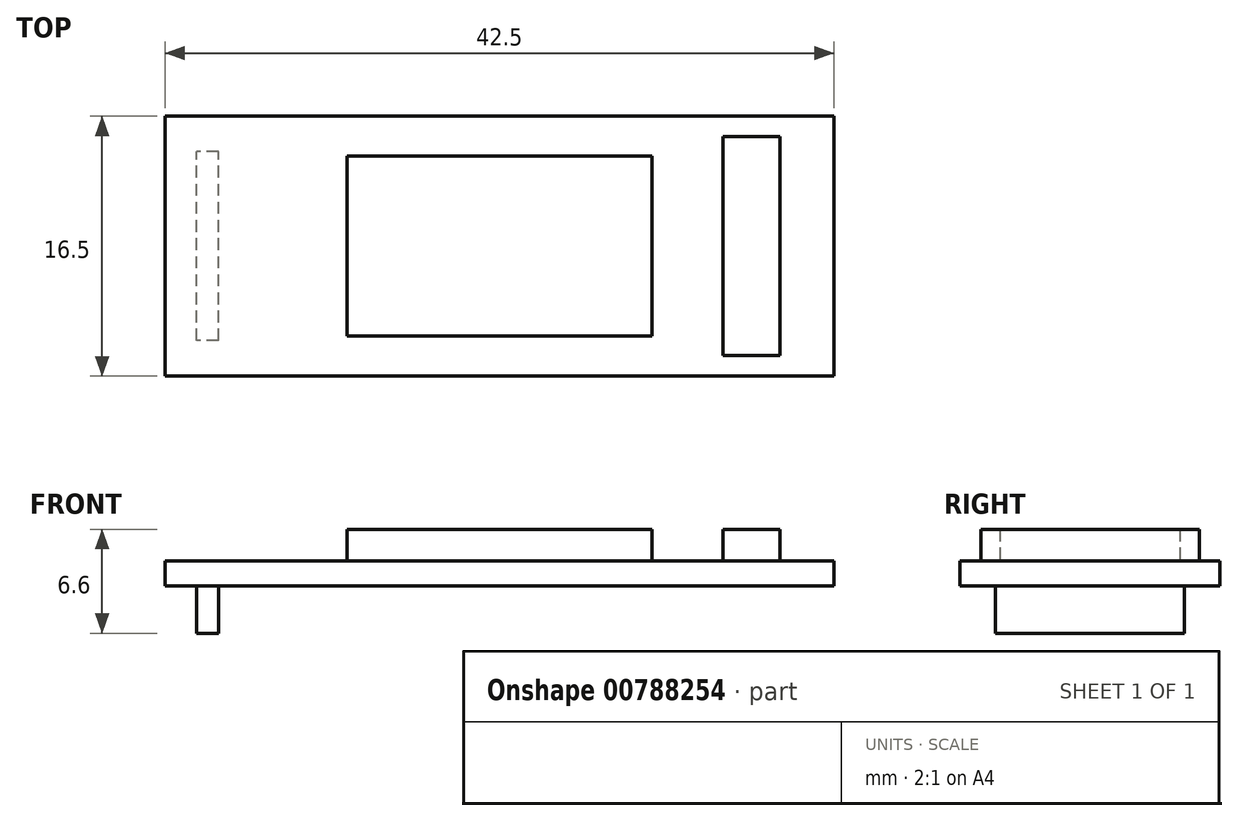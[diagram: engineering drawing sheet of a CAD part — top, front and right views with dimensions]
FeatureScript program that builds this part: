
annotation { "Feature Type Name" : "Feature", "Feature Type Description" : "" }
export const myFeature = defineFeature(function(context is Context, id is Id, definition is map)
    precondition{}
    {
        {
            var Q0;
            Q0=qCreatedBy(makeId("Top.planeOp"),FACE);
            var sketch = newSketch(context, id + "F0", { "sketchPlane" : qUnion([Q0])});
            skLineSegment(sketch, "E0.bottom", {"start": v(21.25, 8.25) * mm, "end": v(-21.25, 8.25) * mm});
            skLineSegment(sketch, "E0.top", {"start": v(21.25, -8.25) * mm, "end": v(-21.25, -8.25) * mm});
            skLineSegment(sketch, "E0.left", {"start": v(21.25, 8.25) * mm, "end": v(21.25, -8.25) * mm});
            skLineSegment(sketch, "E0.right", {"start": v(-21.25, 8.25) * mm, "end": v(-21.25, -8.25) * mm});
            skPoint(sketch, "E0.middle", {"position": v(0, 0) * mm});
            skSolve(sketch);
        }
        {
            var Q0;
            Q0=makeQuery(id+"F0.imprint","IMPRINT",FACE,{"disambiguationData":[TD([[makeQuery(id+"F0.imprint","IMPRINT",EDGE,{"derivedFrom":sQuery(id+"F0.wireOp",EDGE,"E0.bottom")}),1.0]])]});
            extrude(context, id + "F1", {"entities" : qUnion([Q0]), "depth" : 1.6 * mm, "offsetDistance" : 25 * mm});
        }
        {
            var Q0;
            Q0=makeQuery(id+"F1.opExtrude","CAP_FACE",FACE,{"disambiguationData":[OSD([sQuery(id+"F0.wireOp",EDGE,"E0.bottom"),sQuery(id+"F0.wireOp",EDGE,"E0.top"),sQuery(id+"F0.wireOp",EDGE,"E0.left"),sQuery(id+"F0.wireOp",EDGE,"E0.right")])],"isStart":false});
            var sketch = newSketch(context, id + "F2", { "sketchPlane" : qUnion([Q0])});
            skLineSegment(sketch, "E1.bottom", {"start": v(9.7, -5.72) * mm, "end": v(-9.7, -5.72) * mm});
            skLineSegment(sketch, "E1.top", {"start": v(9.7, 5.72) * mm, "end": v(-9.7, 5.72) * mm});
            skLineSegment(sketch, "E1.left", {"start": v(9.7, -5.72) * mm, "end": v(9.7, 5.72) * mm});
            skLineSegment(sketch, "E1.right", {"start": v(-9.7, -5.72) * mm, "end": v(-9.7, 5.72) * mm});
            skPoint(sketch, "E1.middle", {"position": v(0, 0) * mm});
            skLineSegment(sketch, "E2.bottom", {"start": v(17.8, 6.94) * mm, "end": v(14.2, 6.94) * mm});
            skLineSegment(sketch, "E2.top", {"start": v(17.8, -6.94) * mm, "end": v(14.2, -6.94) * mm});
            skLineSegment(sketch, "E2.left", {"start": v(17.8, 6.94) * mm, "end": v(17.8, -6.94) * mm});
            skLineSegment(sketch, "E2.right", {"start": v(14.2, 6.94) * mm, "end": v(14.2, -6.94) * mm});
            skPoint(sketch, "E2.middle", {"position": v(16, 0) * mm});
            skSolve(sketch);
        }
        {
            var Q0;
            Q0=makeQuery(id+"F2.imprint","IMPRINT",FACE,{"disambiguationData":[TD([[makeQuery(id+"F2.imprint","IMPRINT",EDGE,{"derivedFrom":sQuery(id+"F2.wireOp",EDGE,"E1.bottom")}),-1.0]])]});
            var Q1;
            Q1=makeQuery(id+"F2.imprint","IMPRINT",FACE,{"disambiguationData":[TD([[makeQuery(id+"F2.imprint","IMPRINT",EDGE,{"derivedFrom":sQuery(id+"F2.wireOp",EDGE,"E2.bottom")}),1.0]])]});
            extrude(context, id + "F3", {"entities" : qUnion([Q0, Q1]), "operationType" : NewBodyOperationType.ADD, "depth" : 2 * mm, "offsetDistance" : 25 * mm});
        }
        {
            var Q0;
            Q0=makeQuery(id+"F1.opExtrude","CAP_FACE",FACE,{"disambiguationData":[OSD([sQuery(id+"F0.wireOp",EDGE,"E0.bottom"),sQuery(id+"F0.wireOp",EDGE,"E0.top"),sQuery(id+"F0.wireOp",EDGE,"E0.left"),sQuery(id+"F0.wireOp",EDGE,"E0.right")])],"isStart":true});
            var sketch = newSketch(context, id + "F4", { "sketchPlane" : qUnion([Q0])});
            skLineSegment(sketch, "E3.bottom", {"start": v(-17.85, 6) * mm, "end": v(-19.25, 6) * mm});
            skLineSegment(sketch, "E3.top", {"start": v(-17.85, -6) * mm, "end": v(-19.25, -6) * mm});
            skLineSegment(sketch, "E3.left", {"start": v(-17.85, 6) * mm, "end": v(-17.85, -6) * mm});
            skLineSegment(sketch, "E3.right", {"start": v(-19.25, 6) * mm, "end": v(-19.25, -6) * mm});
            skPoint(sketch, "E3.middle", {"position": v(-18.55, 0) * mm});
            skSolve(sketch);
        }
        {
            var Q0;
            Q0=makeQuery(id+"F4.imprint","IMPRINT",FACE,{"disambiguationData":[TD([[makeQuery(id+"F4.imprint","IMPRINT",EDGE,{"derivedFrom":sQuery(id+"F4.wireOp",EDGE,"E3.bottom")}),1.0]])]});
            extrude(context, id + "F5", {"entities" : qUnion([Q0]), "operationType" : NewBodyOperationType.ADD, "depth" : 3 * mm, "offsetDistance" : 25 * mm});
        }
    });
